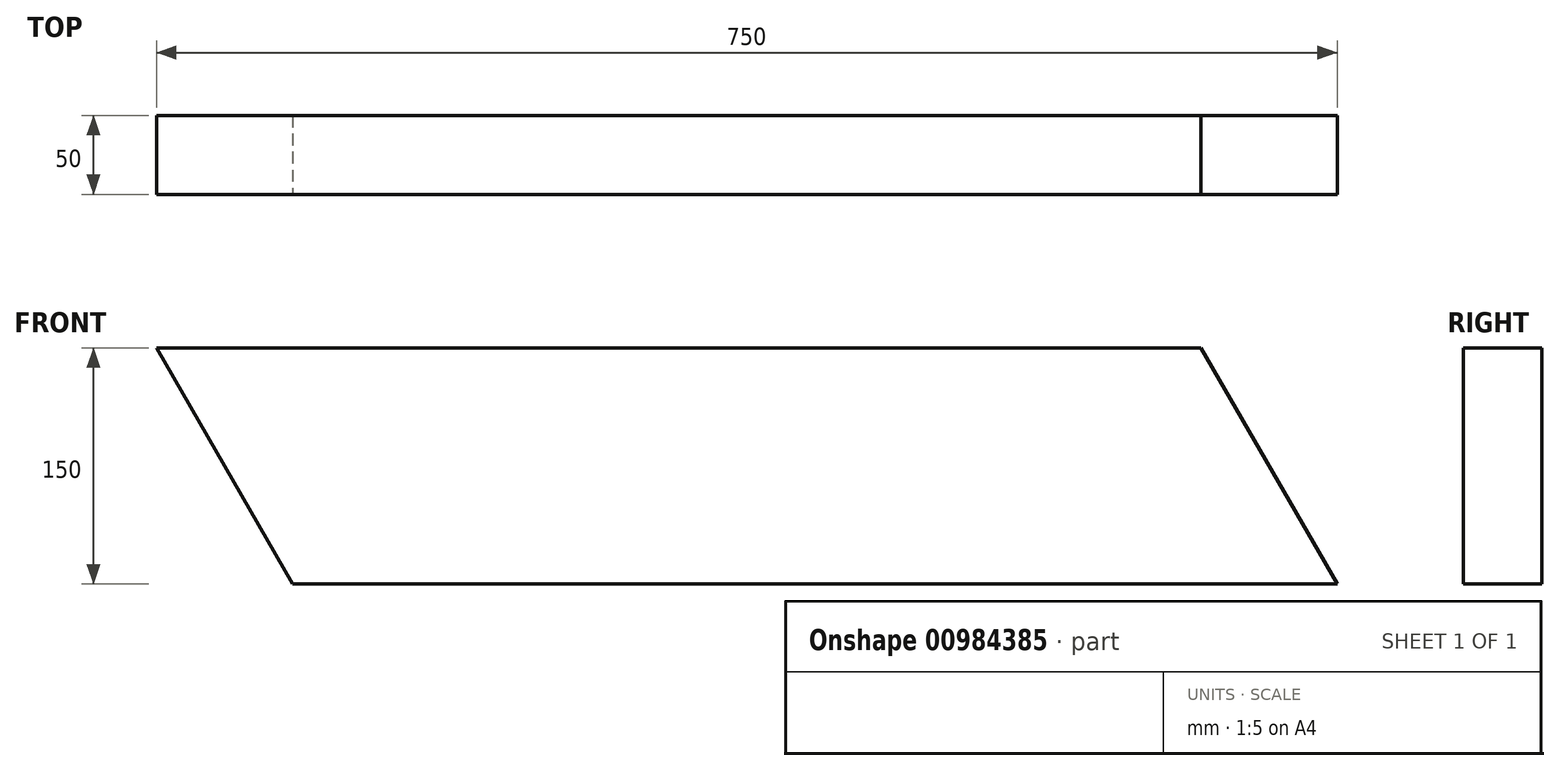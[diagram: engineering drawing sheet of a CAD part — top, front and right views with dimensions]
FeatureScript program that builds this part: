
annotation { "Feature Type Name" : "Feature", "Feature Type Description" : "" }
export const myFeature = defineFeature(function(context is Context, id is Id, definition is map)
    precondition{}
    {
        {
            var Q0;
            Q0=qCreatedBy(makeId("Right.planeOp"),FACE);
            var sketch = newSketch(context, id + "F0", { "sketchPlane" : qUnion([Q0])});
            skLineSegment(sketch, "E0.bottom", {"start": v(25, 75) * mm, "end": v(-25, 75) * mm});
            skLineSegment(sketch, "E0.top", {"start": v(25, -75) * mm, "end": v(-25, -75) * mm});
            skLineSegment(sketch, "E0.left", {"start": v(25, 75) * mm, "end": v(25, -75) * mm});
            skLineSegment(sketch, "E0.right", {"start": v(-25, 75) * mm, "end": v(-25, -75) * mm});
            skPoint(sketch, "E0.middle", {"position": v(0, 0) * mm});
            skSolve(sketch);
        }
        {
            var Q0;
            Q0 = qSketchRegion(id + "F0", true);
            extrude(context, id + "F1", {"entities" : qUnion([Q0]), "endBound" : BoundingType.SYMMETRIC, "depth" : 750 * mm, "offsetDistance" : 25 * mm});
        }
        {
            var Q0;
            Q0=makeQuery(id+"F1.opExtrude","SWEPT_FACE",FACE,{"disambiguationData":[OSD([sQuery(id+"F0.wireOp",EDGE,"E0.right")])]});
            var sketch = newSketch(context, id + "F2", { "sketchPlane" : qUnion([Q0])});
            skLineSegment(sketch, "E1", {"start": v(-375, 75) * mm, "end": v(-288.4, -75) * mm});
            skLineSegment(sketch, "E2", {"start": v(-288.4, -75) * mm, "end": v(-375, -75) * mm});
            skLineSegment(sketch, "E3", {"start": v(-375, -75) * mm, "end": v(-375, 75) * mm});
            skLineSegment(sketch, "E4", {"start": v(375, -75) * mm, "end": v(288.4, 75) * mm});
            skLineSegment(sketch, "E5", {"start": v(288.4, 75) * mm, "end": v(375, 75) * mm});
            skLineSegment(sketch, "E6", {"start": v(375, 75) * mm, "end": v(375, -75) * mm});
            skSolve(sketch);
        }
        {
            var Q0;
            Q0 = qSketchRegion(id + "F2", true);
            extrude(context, id + "F3", {"entities" : qUnion([Q0]), "operationType" : NewBodyOperationType.REMOVE, "endBound" : BoundingType.THROUGH_ALL, "oppositeDirection" : true, "depth" : 25 * mm, "offsetDistance" : 25 * mm});
        }
    });
